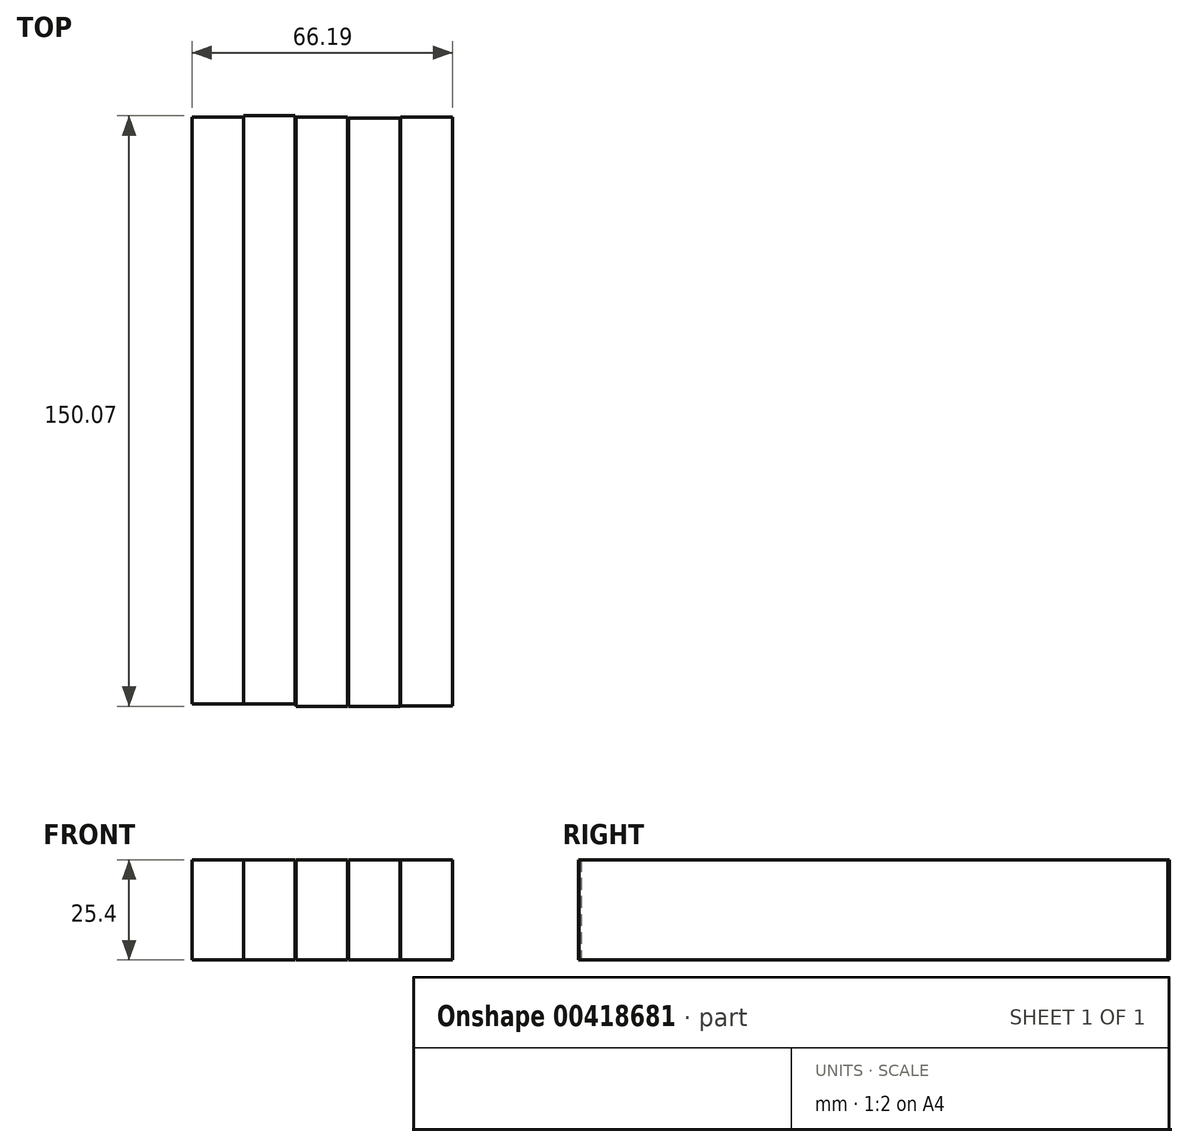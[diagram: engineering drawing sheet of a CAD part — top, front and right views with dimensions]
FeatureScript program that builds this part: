
annotation { "Feature Type Name" : "Feature", "Feature Type Description" : "" }
export const myFeature = defineFeature(function(context is Context, id is Id, definition is map)
    precondition{}
    {
        {
            var Q0;
            Q0=qCreatedBy(makeId("Top.planeOp"),FACE);
            var sketch = newSketch(context, id + "F0", { "sketchPlane" : qUnion([Q0])});
            skLineSegment(sketch, "E0.bottom", {"start": v(-76.39, 76.4) * mm, "end": v(-63.34, 76.4) * mm});
            skLineSegment(sketch, "E0.top", {"start": v(-76.39, -72.73) * mm, "end": v(-63.34, -72.73) * mm});
            skLineSegment(sketch, "E0.left", {"start": v(-76.39, 76.4) * mm, "end": v(-76.39, -72.73) * mm});
            skLineSegment(sketch, "E0.right", {"start": v(-63.34, 76.4) * mm, "end": v(-63.34, -72.73) * mm});
            skSolve(sketch);
        }
        {
            var Q0;
            Q0=qCreatedBy(makeId("Top.planeOp"),FACE);
            var sketch = newSketch(context, id + "F1", { "sketchPlane" : qUnion([Q0])});
            skLineSegment(sketch, "E1.bottom", {"start": v(-63.34, 76.72) * mm, "end": v(-50.29, 76.72) * mm});
            skLineSegment(sketch, "E1.top", {"start": v(-63.34, -72.73) * mm, "end": v(-50.29, -72.73) * mm});
            skLineSegment(sketch, "E1.left", {"start": v(-63.34, 76.72) * mm, "end": v(-63.34, -72.73) * mm});
            skLineSegment(sketch, "E1.right", {"start": v(-50.29, 76.72) * mm, "end": v(-50.29, -72.73) * mm});
            skSolve(sketch);
        }
        {
            var Q0;
            Q0=qCreatedBy(makeId("Top.planeOp"),FACE);
            var sketch = newSketch(context, id + "F2", { "sketchPlane" : qUnion([Q0])});
            skLineSegment(sketch, "E2.bottom", {"start": v(-36.61, 76.1) * mm, "end": v(-23.56, 76.1) * mm});
            skLineSegment(sketch, "E2.top", {"start": v(-36.61, -73.35) * mm, "end": v(-23.56, -73.35) * mm});
            skLineSegment(sketch, "E2.left", {"start": v(-36.61, 76.1) * mm, "end": v(-36.61, -73.35) * mm});
            skLineSegment(sketch, "E2.right", {"start": v(-23.56, 76.1) * mm, "end": v(-23.56, -73.35) * mm});
            skSolve(sketch);
        }
        {
            var Q0;
            Q0=qCreatedBy(makeId("Top.planeOp"),FACE);
            var sketch = newSketch(context, id + "F3", { "sketchPlane" : qUnion([Q0])});
            skLineSegment(sketch, "E3.bottom", {"start": v(-36.93, 76.4) * mm, "end": v(-49.98, 76.4) * mm});
            skLineSegment(sketch, "E3.top", {"start": v(-36.93, -73.35) * mm, "end": v(-49.98, -73.35) * mm});
            skLineSegment(sketch, "E3.left", {"start": v(-36.93, 76.4) * mm, "end": v(-36.93, -73.35) * mm});
            skLineSegment(sketch, "E3.right", {"start": v(-49.98, 76.4) * mm, "end": v(-49.98, -73.35) * mm});
            skSolve(sketch);
        }
        {
            var Q0;
            Q0=qCreatedBy(makeId("Top.planeOp"),FACE);
            var sketch = newSketch(context, id + "F4", { "sketchPlane" : qUnion([Q0])});
            skLineSegment(sketch, "E4.bottom", {"start": v(-23.4, 76.33) * mm, "end": v(-10.2, 76.33) * mm});
            skLineSegment(sketch, "E4.top", {"start": v(-23.4, -73.29) * mm, "end": v(-10.2, -73.29) * mm});
            skLineSegment(sketch, "E4.left", {"start": v(-23.4, 76.33) * mm, "end": v(-23.4, -73.29) * mm});
            skLineSegment(sketch, "E4.right", {"start": v(-10.2, 76.33) * mm, "end": v(-10.2, -73.29) * mm});
            skSolve(sketch);
        }
        {
            var Q0;
            Q0 = qSketchRegion(id + "F0", true);
            var Q1;
            Q1 = qSketchRegion(id + "F1", true);
            var Q2;
            Q2 = qSketchRegion(id + "F2", true);
            var Q3;
            Q3 = qSketchRegion(id + "F3", true);
            var Q4;
            Q4 = qSketchRegion(id + "F4", true);
            extrude(context, id + "F5", {"entities" : qUnion([Q0, Q1, Q2, Q3, Q4]), "depth" : 25.4 * mm});
        }
    });
